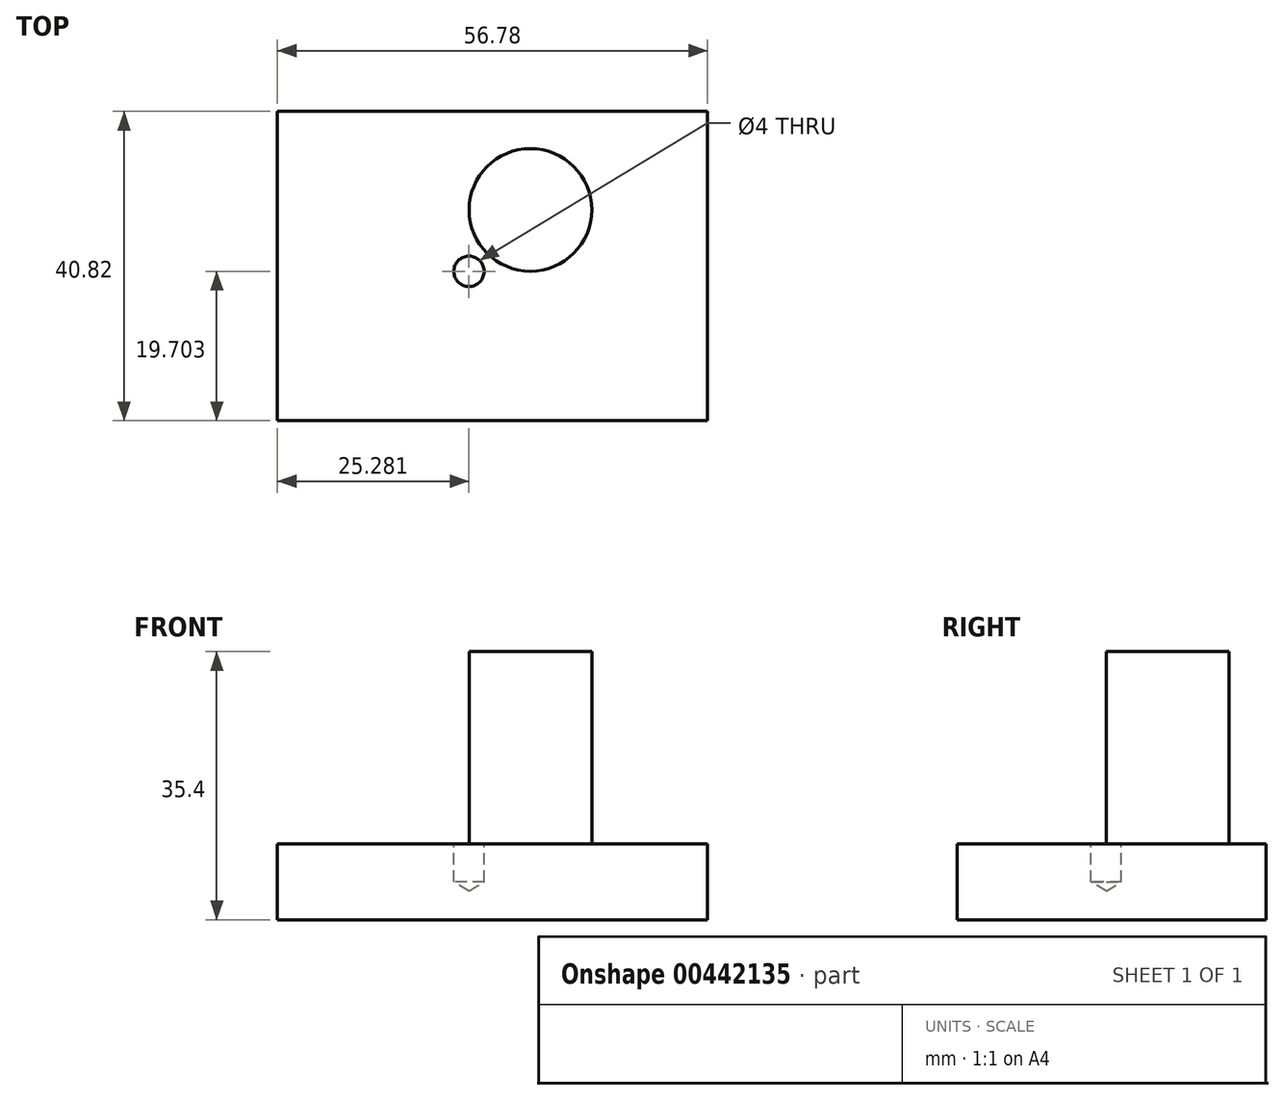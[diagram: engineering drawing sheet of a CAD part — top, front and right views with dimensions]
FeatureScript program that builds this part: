
annotation { "Feature Type Name" : "Feature", "Feature Type Description" : "" }
export const myFeature = defineFeature(function(context is Context, id is Id, definition is map)
    precondition{}
    {
        {
            var Q0;
            Q0=qCreatedBy(makeId("Top.planeOp"),FACE);
            var sketch = newSketch(context, id + "F0", { "sketchPlane" : qUnion([Q0])});
            skLineSegment(sketch, "E0.bottom", {"start": v(0, 0) * mm, "end": v(56.78, 0) * mm});
            skLineSegment(sketch, "E0.top", {"start": v(0, 40.82) * mm, "end": v(56.78, 40.82) * mm});
            skLineSegment(sketch, "E0.left", {"start": v(0, 0) * mm, "end": v(0, 40.82) * mm});
            skLineSegment(sketch, "E0.right", {"start": v(56.78, 0) * mm, "end": v(56.78, 40.82) * mm});
            skSolve(sketch);
        }
        {
            var Q0;
            Q0=makeQuery(id+"F0.imprint","IMPRINT",FACE,{"disambiguationData":[TD([[makeQuery(id+"F0.imprint","IMPRINT",EDGE,{"derivedFrom":sQuery(id+"F0.wireOp",EDGE,"E0.bottom")}),1.0]])]});
            extrude(context, id + "F1", {"entities" : qUnion([Q0]), "depth" : 10 * mm});
        }
        {
            var Q0;
            Q0=makeQuery(id+"F1.opExtrude","CAP_FACE",FACE,{"disambiguationData":[OSD([sQuery(id+"F0.wireOp",EDGE,"E0.bottom"),sQuery(id+"F0.wireOp",EDGE,"E0.top"),sQuery(id+"F0.wireOp",EDGE,"E0.left"),sQuery(id+"F0.wireOp",EDGE,"E0.right")])],"isStart":false});
            var sketch = newSketch(context, id + "F2", { "sketchPlane" : qUnion([Q0])});
            skPoint(sketch, "E1", {"position": v(25.28, 19.7) * mm});
            skSolve(sketch);
        }
        {
            var Q0;
            Q0=sQuery(id+"F2.wireOp",VERTEX,"E1");
            var Q1;
            Q1=makeQuery(id+"F1.opExtrude","SWEPT_BODY",BODY,{"disambiguationData":[OSD([sQuery(id+"F0.wireOp",EDGE,"E0.bottom"),sQuery(id+"F0.wireOp",EDGE,"E0.top"),sQuery(id+"F0.wireOp",EDGE,"E0.left"),sQuery(id+"F0.wireOp",EDGE,"E0.right")])]});
            hole(context, id + "F3", {"style" : HoleStyle.SIMPLE, "endStyle" : HoleEndStyle.BLIND, "holeDiameter" : 4 * mm, "holeDepth" : 5 * mm, "isTappedThrough" : true, "tappedDepth" : 12.7 * mm, "tapClearance" : 3, "locations" : qUnion([Q0]), "scope" : qUnion([Q1])});
        }
        {
            var Q0;
            Q0=makeQuery(id+"F1.opExtrude","CAP_FACE",FACE,{"disambiguationData":[OSD([sQuery(id+"F0.wireOp",EDGE,"E0.bottom"),sQuery(id+"F0.wireOp",EDGE,"E0.top"),sQuery(id+"F0.wireOp",EDGE,"E0.left"),sQuery(id+"F0.wireOp",EDGE,"E0.right")])],"isStart":false});
            var sketch = newSketch(context, id + "F4", { "sketchPlane" : qUnion([Q0])});
            skCircle(sketch, "E2", {"center": v(33.4, 27.8) * mm, "radius": 8.09 * mm});
            skSolve(sketch);
        }
        {
            var Q0;
            Q0 = qSketchRegion(id + "F4", true);
            extrude(context, id + "F5", {"entities" : qUnion([Q0]), "operationType" : NewBodyOperationType.ADD, "depth" : 25.4 * mm, "offsetDistance" : 25.4 * mm});
        }
    });
